# Revit family: HVAC_Ortal_Fireplace_Wilderness_Corner2
name_source: partatom
category: Specialty Equipment
units: mm (PartAtom-declared; Revit-internal decimal feet)

## family parameters
Cut with Voids When Loaded = Yes
Host = Face
OmniClass Number = 23.40.20.34.14
OmniClass Title = Fireplaces
Part Type = Normal
Room Calculation Point = No
Round Connector Dimension = Use Diameter
Shared = No

## types (1)
- Not a Type - Laod Type Catalog!
    Apparent Load = 750 VA
    Assembly Code = E1090400
    Certification = ANSI Z21.88/CSA 2.33-2019
    Current = 15 A
    Default Elevation = 0"
    Depth = 25 3/4"
    Description = Wilderness Type Corner Fireplace
    Edition number = 1
    Efficiency = 79.7%
    Frequency = 60 Hz
    Gas Flow = 0 GPM
    Gas Inlet Diameter = 1/2"
    Gas Type = Gas : Natural Gas
    Height = 43 7/8"
    Interior Material = Ortal - Panel - Black Reflective Glass
    Keynote = 15500
    Manufacturer = Ortal
    Model = Model not specified - Load Type Catalog!
    Number of Poles = 3
    Power Factor = 0.8
    Product Guid = Product Guid not specified - Load Type Catalog!
    Product Material = Ortal - Stainless Steel - Black
    Product data url = Product data url not specified - Load Type Catalog!
    Total Heating Capacity = 32768.0 Btu/h
    URL = https://www.ortalheat.com
    Vent = 5x8 co-axial direct vent pipe (5” interior, 8” exterior)
    Viewing Area Height = 23 13/16"
    Viewing Area Side Length = 19 7/8"
    Viewing Area Width = 28 1/4"
    Voltage = 120 V
    Weight = 347.00 lbf
    Width = 33 1/4"
    z_25H = Yes
    z_44 = No
    z_44H = No
    z_51 = No
    z_51H = No
    z_60 = No
    z_60H = No
    z_68 = No
    z_68H = No
    z_77 = No
    z_77H = No
    z_Array Number = 14
    z_Back L Profile = No
    z_Back L Profile 44 = No
    z_Back L Profile Angle = 40.00°
    z_Back L Profile Offset = 17 1/8"
    z_Back L Profile Top = 3 5/16"
    z_Back Profile DI Length = 13 5/16"
    z_Back Profile DI Offset = 30 7/16"
    z_Bottom = 4 1/2"
    z_Cutout Offset = 1 3/8"
    z_Double Glass = Yes
    z_Frame Thickness = 3/16"
    z_Gas Type 1 = Gas : Natural Gas
    z_Gas Type 2 = Gas : Propane
    z_Glass Depth = 2 1/2"
    z_HB Depth = 1"
    z_Screen = No
    z_Side Array number = 7
    z_Side L DI Length = 17 3/4"
    z_Side L Profile Angle = 30.00°
    z_Side L Profile Bottom = 2"
    z_Side L Profile Front = 2"
    z_Side L Profile Top = 2"
    z_Sides Height = 7 5/16"
    z_Top = 7 5/16"
    z_Top Overlap = No
    z_Vent Depth = 16 3/8"
    z_Vent Width = 15 15/16"

## geometry (parser evidence)
native form markers: Sweep x9
no freeform markers — native parametric forms only
